# Revit family: P200921MX-031c_MFI2570FE_BW
name_source: partatom
category: Specialty Equipment
units: mm (PartAtom-declared; Revit-internal decimal feet)

## family parameters
Always vertical = No
Cut with Voids When Loaded = No
Enable Cutting in Views = No
Maintain Annotation Orientation = No
Part Type = Normal
Room Calculation Point = No
Round Connector Dimension = Use Diameter
Shared = No
Work Plane-Based = No

## types (2) — shared parameters
Amps = 0 A
Clearance Material = ARCAT - Clearance
Default Elevation = 0"
Depth = 35 1/4"
Description = 36- Inch Wide French Door Refrigerator with PowerCold® Feature - 25 Cu. Ft.
Réfrigérateur à portes françaises avec fonction PowerCold®, 36 po, 25 pi3
Dimension Guide = http://access.whirlpool.com Guide&sku=MFI2570FEW&language=EN
http://access.whirlpool.com Guide&sku=MFI2570FEW&language=EN
Energy Guide = http://access.whirlpool.com Guide&sku=MFI2570FEW&language=EN
http://access.whirlpool.com Guide&sku=MFI2570FEW&language=FR
Family Name = Refrigeration
Feature 1 = Fingerprint Resistant Stainless Steel
Acier inoxydable résistant aux traces de doigts
Feature 2 = PowerCold® Feature
Fonction PowerCold™
Feature 3 = Temperature-Controlled Wide-N-Fresh™ Deli Drawer
Tiroir à charcuterie à température contrôlée Wide-N-Fresh™
Glass Material = ARCAT - Glass - Black
Height = 70 1/8"
Manufacturer = Maytag
Voltage = 0 V
Width = 35 5/8"

## per-type parameters (varying)
| type | Accent Material | Body Material | Display Panel Material | Door Material | Handle Material |
| MFI2570FEW | ARCAT - Metal - Steel - White | ARCAT - Metal - Steel - White | ARCAT - Metal - Steel - Stainless - Grey | ARCAT - Metal - Steel - White | ARCAT - Metal - Steel - White |
| MFI2570FEB | ARCAT - Metal - Aluminum - Light | ARCAT - Metal - Steel - Black | ARCAT - Metal - Steel - Black - Light | ARCAT - Metal - Steel - Black | ARCAT - Metal - Steel - Black - Dark |

note: column(s) folded — value = type name in every type: Model

## geometry (parser evidence)
native form markers: Sweep x3
no freeform markers — native parametric forms only
